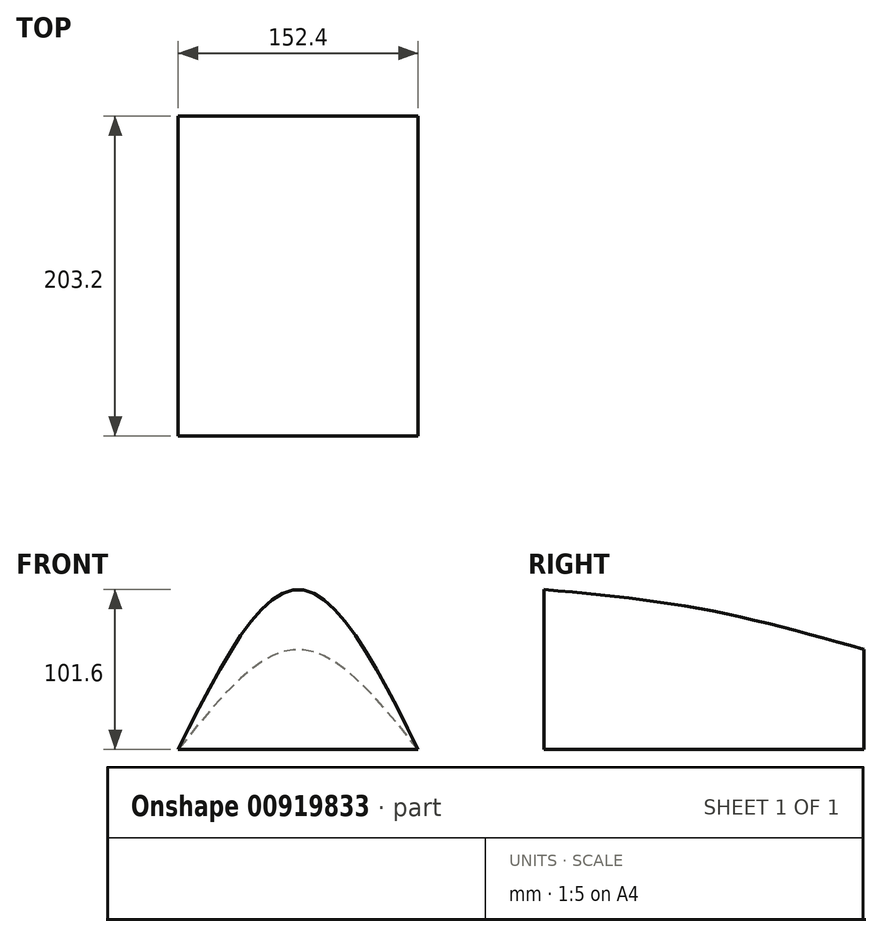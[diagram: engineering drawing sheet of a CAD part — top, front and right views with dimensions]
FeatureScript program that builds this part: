
annotation { "Feature Type Name" : "Feature", "Feature Type Description" : "" }
export const myFeature = defineFeature(function(context is Context, id is Id, definition is map)
    precondition{}
    {
        {
            var Q0;
            Q0=qCreatedBy(makeId("Right.planeOp"),FACE);
            var sketch = newSketch(context, id + "F0", { "sketchPlane" : qUnion([Q0])});
            skLineSegment(sketch, "E0", {"start": v(0, 0) * mm, "end": v(-101.6, 0) * mm, "construction": true});
            skLineSegment(sketch, "E1", {"start": v(0, 0) * mm, "end": v(101.6, 0) * mm, "construction": true});
            skLineSegment(sketch, "E2", {"start": v(101.6, 0) * mm, "end": v(101.6, 63.5) * mm, "construction": true});
            skLineSegment(sketch, "E3", {"start": v(0, 0) * mm, "end": v(0, 88.9) * mm, "construction": true});
            skLineSegment(sketch, "E4", {"start": v(-101.6, 0) * mm, "end": v(-101.6, 101.6) * mm, "construction": true});
            skFitSpline(sketch, "E5", {"points": [v(-101.6, 101.6) * mm, v(0, 88.9) * mm, v(101.6, 63.5) * mm], "startDerivative": vector(204.92, -19.34) * mm, "endDerivative": vector(201.48, -56.8) * mm, "construction": true});
            skSolve(sketch);
        }
        {
            var Q0;
            Q0=qCreatedBy(makeId("Top.planeOp"),FACE);
            var sketch = newSketch(context, id + "F1", { "sketchPlane" : qUnion([Q0])});
            skPoint(sketch, "E6.0", {"position": v(0, -101.6) * mm});
            skPoint(sketch, "E7.0", {"position": v(0, 101.6) * mm});
            skLineSegment(sketch, "E8.bottom", {"start": v(-76.2, -101.6) * mm, "end": v(76.2, -101.6) * mm, "construction": true});
            skLineSegment(sketch, "E8.top", {"start": v(-76.2, 101.6) * mm, "end": v(76.2, 101.6) * mm, "construction": true});
            skLineSegment(sketch, "E8.left", {"start": v(-76.2, -101.6) * mm, "end": v(-76.2, 101.6) * mm, "construction": true});
            skLineSegment(sketch, "E8.right", {"start": v(76.2, -101.6) * mm, "end": v(76.2, 101.6) * mm, "construction": true});
            skPoint(sketch, "E8.middle", {"position": v(0, 0) * mm});
            skSolve(sketch);
        }
        {
            var Q0;
            Q0=qCreatedBy(makeId("Front.planeOp"),FACE);
            var Q1;
            Q1=sQuery(id+"F1.wireOp",VERTEX,"E6.0");
            cPlane(context, id + "F2", {"entities" : qUnion([Q0, Q1]), "cplaneType" : CPlaneType.PLANE_POINT, "offset" : 25.4 * mm, "width" : 152.4 * mm, "height" : 152.4 * mm});
        }
        {
            var Q0;
            Q0=qCreatedBy(id+"F2.planeOp",FACE);
            var sketch = newSketch(context, id + "F3", { "sketchPlane" : qUnion([Q0])});
            skPoint(sketch, "E9.0", {"position": v(-76.2, 0) * mm});
            skPoint(sketch, "E10.0", {"position": v(0, 101.6) * mm});
            skPoint(sketch, "E11.0", {"position": v(76.2, 0) * mm});
            skFitSpline(sketch, "E12", {"points": [v(-76.2, 0) * mm, v(0, 101.6) * mm, v(76.2, 0) * mm], "startDerivative": vector(152.4, 304.8) * mm, "endDerivative": vector(152.4, -304.8) * mm});
            skLineSegment(sketch, "E13", {"start": v(-76.2, 0) * mm, "end": v(76.2, 0) * mm});
            skFitSpline(sketch, "E14.0", {"points": [v(-78.1, 0) * mm, v(-74.92, 6.35) * mm, v(-68.56, 19.06) * mm, v(-59.02, 37.55) * mm, v(-49.46, 54.88) * mm, v(-39.87, 70.46) * mm, v(-30.23, 83.73) * mm, v(-22.1, 92.37) * mm, v(-15.5, 97.54) * mm, v(-10.44, 100.47) * mm, v(-6.14, 102.02) * mm, v(-2.64, 102.66) * mm, v(0, 102.83) * mm, v(2.64, 102.66) * mm, v(6.14, 102.02) * mm, v(10.44, 100.47) * mm, v(15.5, 97.54) * mm, v(22.1, 92.37) * mm, v(30.23, 83.73) * mm, v(39.87, 70.46) * mm, v(49.46, 54.88) * mm, v(59.02, 37.55) * mm, v(68.56, 19.06) * mm, v(74.92, 6.35) * mm, v(78.1, 0) * mm], "construction": true});
            skLineSegment(sketch, "E15", {"start": v(76.2, 0) * mm, "end": v(83.7, 0) * mm, "construction": true});
            skLineSegment(sketch, "E16", {"start": v(-76.2, 0) * mm, "end": v(-89.02, 0) * mm, "construction": true});
            skSolve(sketch);
        }
        {
            var Q0;
            Q0=qCreatedBy(makeId("Front.planeOp"),FACE);
            var sketch = newSketch(context, id + "F4", { "sketchPlane" : qUnion([Q0])});
            skPoint(sketch, "E17.0", {"position": v(0, 88.9) * mm});
            skPoint(sketch, "E18.0", {"position": v(76.2, 0) * mm});
            skPoint(sketch, "E19.0", {"position": v(-76.2, 0) * mm});
            skFitSpline(sketch, "E20", {"points": [v(-76.2, 0) * mm, v(0, 88.9) * mm, v(76.2, 0) * mm], "startDerivative": vector(152.4, 266.7) * mm, "endDerivative": vector(152.4, -266.7) * mm});
            skLineSegment(sketch, "E21", {"start": v(-76.2, 0) * mm, "end": v(76.2, 0) * mm});
            skSolve(sketch);
        }
        {
            var Q0;
            Q0=qCreatedBy(makeId("Front.planeOp"),FACE);
            var Q1;
            Q1=sQuery(id+"F1.wireOp",VERTEX,"E8.top.end");
            cPlane(context, id + "F5", {"entities" : qUnion([Q0, Q1]), "cplaneType" : CPlaneType.PLANE_POINT, "offset" : 25.4 * mm, "width" : 152.4 * mm, "height" : 152.4 * mm});
        }
        {
            var Q0;
            Q0=qCreatedBy(id+"F5.planeOp",FACE);
            var sketch = newSketch(context, id + "F6", { "sketchPlane" : qUnion([Q0])});
            skPoint(sketch, "E22.0", {"position": v(76.2, 0) * mm});
            skPoint(sketch, "E23.0", {"position": v(-76.2, 0) * mm});
            skPoint(sketch, "E24.0", {"position": v(0, 63.5) * mm});
            skFitSpline(sketch, "E25", {"points": [v(76.2, 0) * mm, v(0, 63.5) * mm, v(-76.2, 0) * mm], "startDerivative": vector(-152.4, 190.5) * mm, "endDerivative": vector(-152.4, -190.5) * mm});
            skLineSegment(sketch, "E26", {"start": v(76.2, 0) * mm, "end": v(-76.2, 0) * mm});
            skSolve(sketch);
        }
        {
            var Q0;
            Q0=makeQuery(id+"F3.imprint","IMPRINT",FACE,{"disambiguationData":[TD([[makeQuery(id+"F3.imprint","IMPRINT",EDGE,{"derivedFrom":sQuery(id+"F3.wireOp",EDGE,"E12")}),-1.0]])]});
            var Q1;
            Q1=makeQuery(id+"F4.imprint","IMPRINT",FACE,{"disambiguationData":[TD([[makeQuery(id+"F4.imprint","IMPRINT",EDGE,{"derivedFrom":sQuery(id+"F4.wireOp",EDGE,"E20")}),-1.0]])]});
            var Q2;
            Q2=makeQuery(id+"F6.imprint","IMPRINT",FACE,{"disambiguationData":[TD([[makeQuery(id+"F6.imprint","IMPRINT",EDGE,{"derivedFrom":sQuery(id+"F6.wireOp",EDGE,"E25")}),1.0]])]});
            loft(context, id + "F7", {"sheetProfilesArray" : [{ "sheetProfileEntities" : qUnion([Q0]) }, { "sheetProfileEntities" : qUnion([Q1]) }, { "sheetProfileEntities" : qUnion([Q2]) }]});
        }
    });
